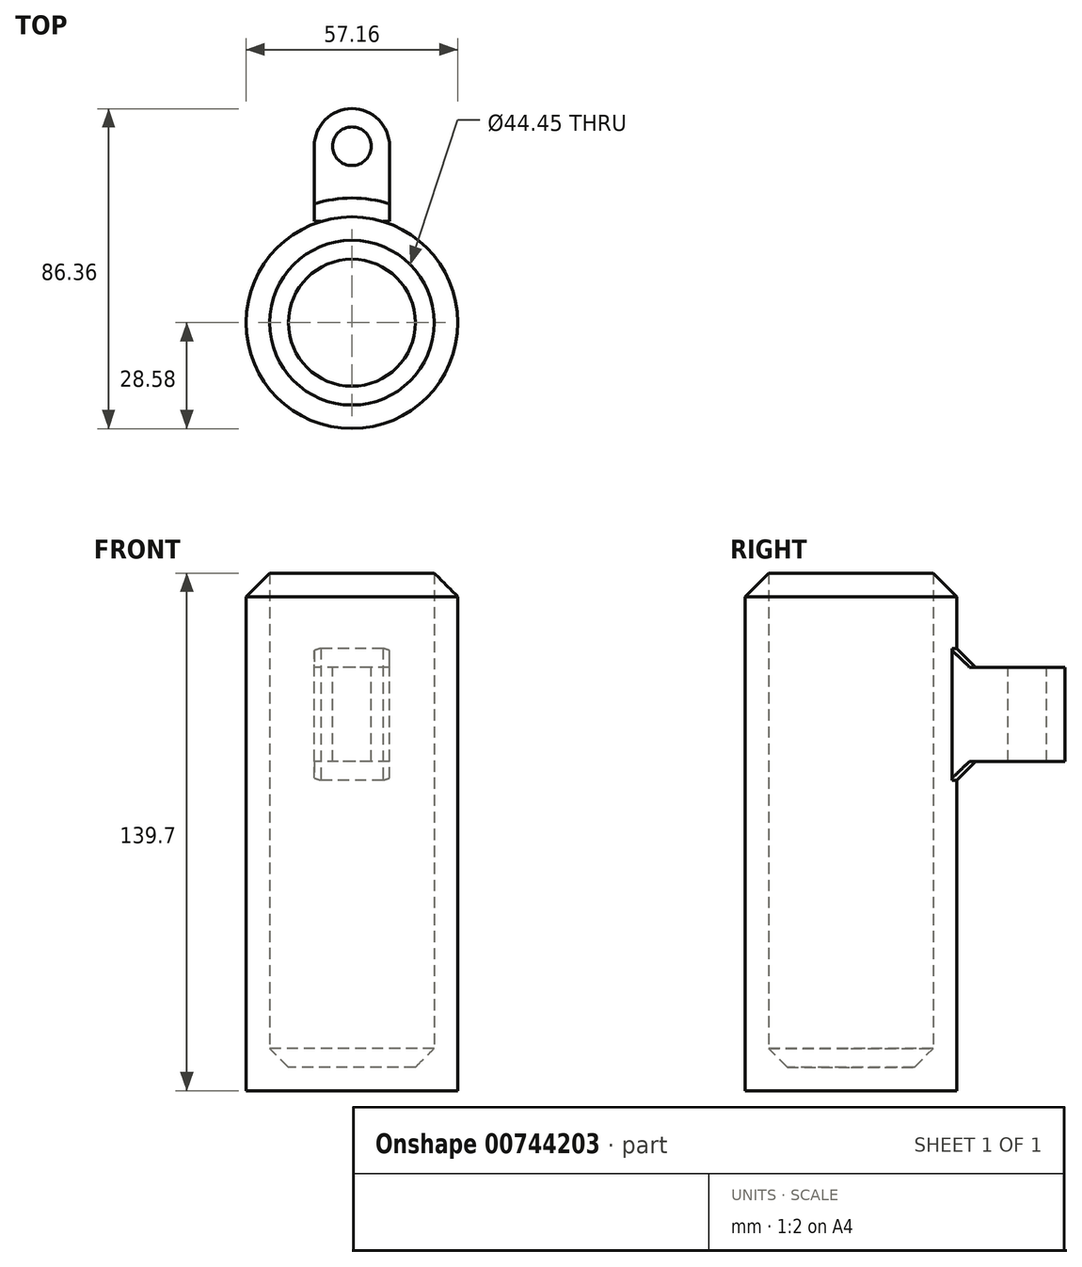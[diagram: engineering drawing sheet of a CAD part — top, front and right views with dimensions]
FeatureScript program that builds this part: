
annotation { "Feature Type Name" : "Feature", "Feature Type Description" : "" }
export const myFeature = defineFeature(function(context is Context, id is Id, definition is map)
    precondition{}
    {
        {
            var Q0;
            Q0=qCreatedBy(makeId("Top.planeOp"),FACE);
            var sketch = newSketch(context, id + "F0", { "sketchPlane" : qUnion([Q0])});
            skCircle(sketch, "E0", {"center": v(0, 0) * mm, "radius": 28.58 * mm});
            skSolve(sketch);
        }
        {
            var Q0;
            Q0=makeQuery(id+"F0.imprint","IMPRINT",FACE,{"disambiguationData":[TD([[makeQuery(id+"F0.imprint","IMPRINT",EDGE,{"derivedFrom":sQuery(id+"F0.wireOp",EDGE,"E0")}),1.0]])]});
            extrude(context, id + "F1", {"entities" : qUnion([Q0]), "depth" : 139.7 * mm, "offsetDistance" : 25.4 * mm});
        }
        {
            var Q0;
            Q0=makeQuery(id+"F1.opExtrude","CAP_FACE",FACE,{"disambiguationData":[OSD([sQuery(id+"F0.wireOp",EDGE,"E0")])],"isStart":false});
            shell(context, id + "F2", {"entities" : qUnion([Q0]), "thickness" : 6.35 * mm});
        }
        {
            var Q0;
            Q0=qCreatedBy(makeId("Top.planeOp"),FACE);
            cPlane(context, id + "F3", {"entities" : qUnion([Q0]), "cplaneType" : CPlaneType.OFFSET, "offset" : 114.3 * mm, "width" : 152.4 * mm, "height" : 152.4 * mm});
        }
        {
            var Q0;
            Q0=qCreatedBy(id+"F3.planeOp",FACE);
            var sketch = newSketch(context, id + "F4", { "sketchPlane" : qUnion([Q0])});
            skCircle(sketch, "E1", {"center": v(0, 47.62) * mm, "radius": 5.2 * mm});
            skCircle(sketch, "E2", {"center": v(0, 47.62) * mm, "radius": 10.16 * mm});
            skLineSegment(sketch, "E3", {"start": v(0, 47.62) * mm, "end": v(-10.16, 47.62) * mm});
            skLineSegment(sketch, "E4", {"start": v(-10.16, 47.62) * mm, "end": v(-10.16, 27.3) * mm});
            skLineSegment(sketch, "E5.MirrorCS", {"start": v(10.16, 47.62) * mm, "end": v(10.16, 27.3) * mm});
            skLineSegment(sketch, "E6", {"start": v(-10.16, 27.3) * mm, "end": v(10.16, 27.3) * mm});
            skSolve(sketch);
        }
        {
            var Q0;
            Q0=qSketchRegion(id+"F4",true);
            extrude(context, id + "F5", {"entities" : qUnion([Q0]), "oppositeDirection" : true, "depth" : 25.4 * mm, "offsetDistance" : 25.4 * mm});
        }
        {
            var Q0;
            Q0=makeQuery(id+"F5.opExtrude","SWEPT_BODY",BODY,{"disambiguationData":[OSD([sQuery(id+"F4.wireOp",EDGE,"E1"),sQuery(id+"F4.wireOp",EDGE,"E2"),sQuery(id+"F4.wireOp",EDGE,"E4"),sQuery(id+"F4.wireOp",EDGE,"E5.MirrorCS"),sQuery(id+"F4.wireOp",EDGE,"E6")])]});
            var Q1;
            Q1=makeQuery(id+"F1.opExtrude","SWEPT_BODY",BODY,{"disambiguationData":[OSD([sQuery(id+"F0.wireOp",EDGE,"E0")])]});
            booleanBodies(context, id + "F6", {"operationType" : BooleanOperationType.UNION, "tools" : qUnion([Q0, Q1])});
        }
        {
            var Q0;
            Q0=makeQuery(id+"F1.opExtrude","CAP_EDGE",EDGE,{"disambiguationData":[OSD([sQuery(id+"F0.wireOp",EDGE,"E0")])],"isStart":false});
            chamfer(context, id + "F7", {"entities" : qUnion([Q0]), "width" : 6.35 * mm, "tangentPropagation" : true});
        }
        {
            var Q0;
            Q0=makeQuery(id+"F6.opBoolean","INTERSECT",EDGE,{"derivedFrom":[makeQuery(id+"F5.opExtrude","CAP_FACE",FACE,{"disambiguationData":[OSD([sQuery(id+"F4.wireOp",EDGE,"E1"),sQuery(id+"F4.wireOp",EDGE,"E2"),sQuery(id+"F4.wireOp",EDGE,"E4"),sQuery(id+"F4.wireOp",EDGE,"E5.MirrorCS"),sQuery(id+"F4.wireOp",EDGE,"E6")])],"isStart":true}),makeQuery(id+"F1.opExtrude","SWEPT_FACE",FACE,{"disambiguationData":[OSD([sQuery(id+"F0.wireOp",EDGE,"E0")])]})]});
            var Q1;
            Q1=makeQuery(id+"FK5f2kmZ7Gavp52_2.boolean.opBoolean","INTERSECT",EDGE,{"derivedFrom":[makeQuery(id+"F1.opExtrude","SWEPT_FACE",FACE,{"disambiguationData":[OSD([sQuery(id+"F0.wireOp",EDGE,"E0")])]}),makeQuery(id+"FK5f2kmZ7Gavp52_2.opExtrude","CAP_FACE",FACE,{"disambiguationData":[OSD([sQuery(id+"FyYVerh7Uec2MJB_2.wireOp",EDGE,"BOP3p5xP-4JjG-RjDQ-ucZO-sWsOryHELw3N"),sQuery(id+"FyYVerh7Uec2MJB_2.wireOp",EDGE,"8A7jfMN9-cw69-uJgx-RMdz-U0ODDKvCNGEe"),sQuery(id+"FyYVerh7Uec2MJB_2.wireOp",EDGE,"WRXYRtJ2-xQZK-vpre-eXYv-0XO9ZbJuvgVX"),sQuery(id+"FyYVerh7Uec2MJB_2.wireOp",EDGE,"396sjhhi-fjg6-mvxd-rteL-sxiENpM78ffD"),sQuery(id+"FyYVerh7Uec2MJB_2.wireOp",EDGE,"7YnIvfqC-mKDA-WhrD-OOL3-0WvLCzw3rz9N")])],"isStart":false})]});
            chamfer(context, id + "F8", {"entities" : qUnion([Q0, Q1]), "width" : 5.08 * mm, "tangentPropagation" : true});
        }
        {
            var Q0;
            Q0=makeQuery(id+"F6.opBoolean","INTERSECT",EDGE,{"derivedFrom":[makeQuery(id+"F5.opExtrude","CAP_FACE",FACE,{"disambiguationData":[OSD([sQuery(id+"F4.wireOp",EDGE,"E1"),sQuery(id+"F4.wireOp",EDGE,"E2"),sQuery(id+"F4.wireOp",EDGE,"E4"),sQuery(id+"F4.wireOp",EDGE,"E5.MirrorCS"),sQuery(id+"F4.wireOp",EDGE,"E6")])],"isStart":false}),makeQuery(id+"F1.opExtrude","SWEPT_FACE",FACE,{"disambiguationData":[OSD([sQuery(id+"F0.wireOp",EDGE,"E0")])]})]});
            chamfer(context, id + "F9", {"entities" : qUnion([Q0]), "width" : 5.08 * mm, "tangentPropagation" : true});
        }
        {
            var Q0;
            {var subQ0=sQuery(id+"F0.wireOp",EDGE,"E0");Q0=makeQuery(id+"F2.opShell","OFFSET_EDGE",EDGE,{"disambiguationData":[OSD([subQ0]),TDD([makeQuery(id+"F1.opExtrude","CAP_EDGE",EDGE,{"disambiguationData":[OSD([subQ0])],"isStart":true})])]});}
            chamfer(context, id + "F10", {"entities" : qUnion([Q0]), "width" : 5.08 * mm, "tangentPropagation" : true});
        }
    });
